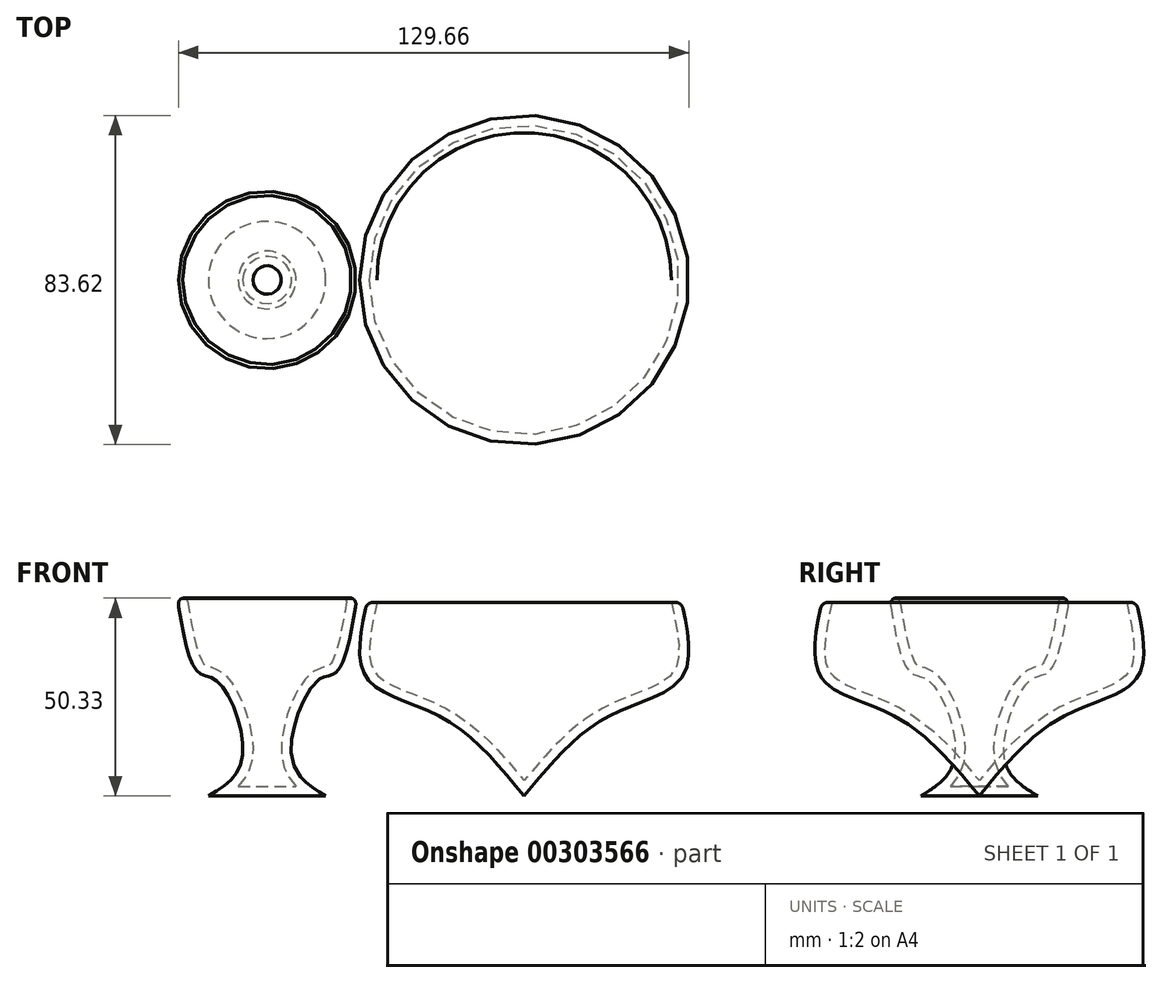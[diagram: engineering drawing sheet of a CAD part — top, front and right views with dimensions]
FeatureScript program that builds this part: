
annotation { "Feature Type Name" : "Feature", "Feature Type Description" : "" }
export const myFeature = defineFeature(function(context is Context, id is Id, definition is map)
    precondition{}
    {
        {
            var Q0;
            Q0=qCreatedBy(makeId("Front.planeOp"),FACE);
            var sketch = newSketch(context, id + "F0", { "sketchPlane" : qUnion([Q0])});
            skLineSegment(sketch, "E0", {"start": v(0, 49.23) * mm, "end": v(40, 49.23) * mm});
            skLineSegment(sketch, "E1", {"start": v(40, 49.23) * mm, "end": v(40, 0) * mm});
            skFitSpline(sketch, "E2", {"points": [v(0, 49.23) * mm, v(0, 30.01) * mm, v(18.95, 20.08) * mm, v(40, 0) * mm], "startDerivative": vector(-15.43, -72.84) * mm, "endDerivative": vector(51.06, -62.5) * mm});
            skSolve(sketch);
        }
        {
            var Q0;
            Q0=makeQuery(id+"F0.imprint","IMPRINT",FACE,{"disambiguationData":[TD([[makeQuery(id+"F0.imprint","IMPRINT",EDGE,{"derivedFrom":sQuery(id+"F0.wireOp",EDGE,"E0")}),-1.0]])]});
            var Q1;
            Q1=sQuery(id+"F0.wireOp",EDGE,"E1");
            revolve(context, id + "F1", {"entities" : qUnion([Q0]), "axis" : qUnion([Q1]), "revolveType" : RevolveType.FULL});
        }
        {
            var Q0;
            Q0=makeQuery(id+"F1.opRevolve","SWEPT_FACE",FACE,{"disambiguationData":[OSD([sQuery(id+"F0.wireOp",EDGE,"E0")])]});
            shell(context, id + "F2", {"entities" : qUnion([Q0]), "thickness" : 2.5 * mm});
        }
        {
            var Q0;
            Q0=makeQuery(id+"F1.opRevolve","SWEPT_EDGE",EDGE,{"disambiguationData":[OSD([sQuery(id+"F0.wireOp",EDGE,"E0"),sQuery(id+"F0.wireOp",EDGE,"E2")])]});
            fillet(context, id + "F3", {"entities" : qUnion([Q0]), "radius" : 2 * mm, "tangentPropagation" : true, "allowEdgeOverflow" : false});
        }
        {
            var Q0;
            Q0=qCreatedBy(makeId("Front.planeOp"),FACE);
            var sketch = newSketch(context, id + "F4", { "sketchPlane" : qUnion([Q0])});
            skLineSegment(sketch, "E3", {"start": v(-25.32, 0) * mm, "end": v(-25.32, 50.41) * mm});
            skLineSegment(sketch, "E4", {"start": v(-25.32, 50.41) * mm, "end": v(-48.2, 50.41) * mm});
            skFitSpline(sketch, "E5", {"points": [v(-48.2, 50.41) * mm, v(-42.85, 31.47) * mm, v(-38.07, 29.27) * mm, v(-31.58, 9.9) * mm, v(-40.2, 0) * mm], "startDerivative": vector(13.83, -83.8) * mm, "endDerivative": vector(-48.34, -30.1) * mm});
            skLineSegment(sketch, "E6", {"start": v(-25.32, 0) * mm, "end": v(-40.2, 0) * mm});
            skSolve(sketch);
        }
        {
            var Q0;
            Q0=makeQuery(id+"F4.imprint","IMPRINT",FACE,{"disambiguationData":[TD([[makeQuery(id+"F4.imprint","IMPRINT",EDGE,{"derivedFrom":sQuery(id+"F4.wireOp",EDGE,"E3")}),1.0]])]});
            var Q1;
            Q1=sQuery(id+"F4.wireOp",EDGE,"E3");
            revolve(context, id + "F5", {"entities" : qUnion([Q0]), "axis" : qUnion([Q1]), "revolveType" : RevolveType.FULL});
        }
        {
            var Q0;
            Q0=makeQuery(id+"F5.opRevolve","SWEPT_FACE",FACE,{"disambiguationData":[OSD([sQuery(id+"F4.wireOp",EDGE,"E4")])]});
            shell(context, id + "F6", {"entities" : qUnion([Q0]), "thickness" : 2.5 * mm});
        }
        {
            var Q0;
            Q0=makeQuery(id+"F5.opRevolve","SWEPT_EDGE",EDGE,{"disambiguationData":[OSD([sQuery(id+"F4.wireOp",EDGE,"E4"),sQuery(id+"F4.wireOp",EDGE,"E5")])]});
            fillet(context, id + "F7", {"entities" : qUnion([Q0]), "radius" : 2 * mm, "tangentPropagation" : true, "rho" : 0.5, "crossSection" : FilletCrossSection.CONIC, "allowEdgeOverflow" : false});
        }
        {
            var Q0;
            Q0=makeQuery(id+"F6.opShell","OFFSET_EDGE",EDGE,{"disambiguationData":[OSD([sQuery(id+"F4.wireOp",EDGE,"E4"),sQuery(id+"F4.wireOp",EDGE,"E5")])]});
            fillet(context, id + "F8", {"entities" : qUnion([Q0]), "radius" : 1 * mm, "tangentPropagation" : true, "allowEdgeOverflow" : false});
        }
    });
